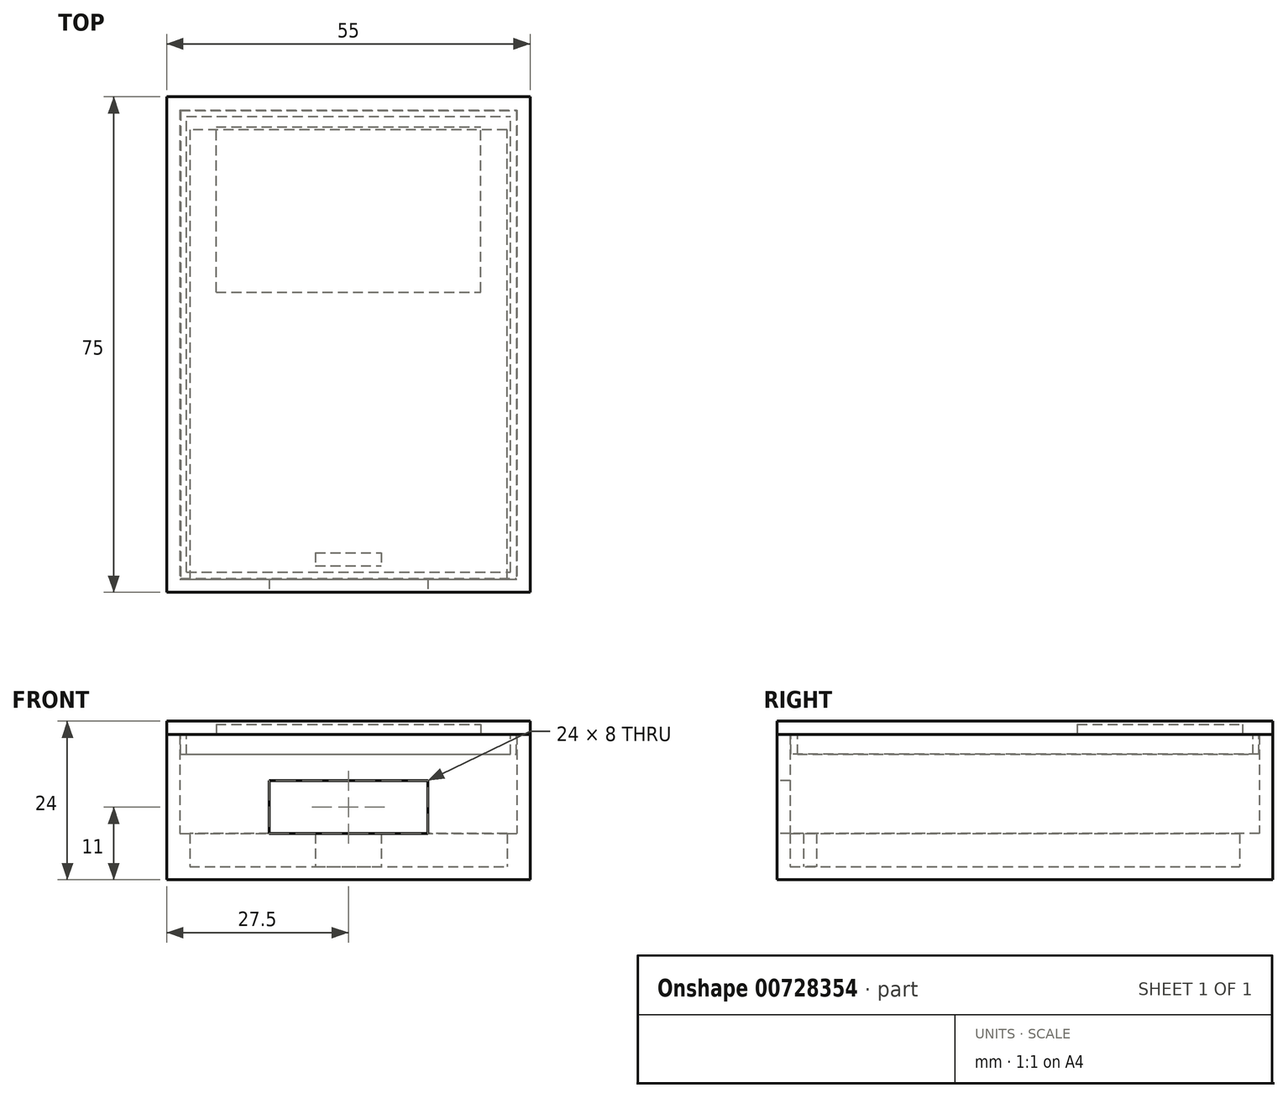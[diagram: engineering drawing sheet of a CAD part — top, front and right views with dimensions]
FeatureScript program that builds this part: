
annotation { "Feature Type Name" : "Feature", "Feature Type Description" : "" }
export const myFeature = defineFeature(function(context is Context, id is Id, definition is map)
    precondition{}
    {
        {
            var Q0;
            Q0=qCreatedBy(makeId("Top.planeOp"),FACE);
            var sketch = newSketch(context, id + "F0", { "sketchPlane" : qUnion([Q0])});
            skLineSegment(sketch, "E0.bottom", {"start": v(-27.5, 37.5) * mm, "end": v(27.5, 37.5) * mm});
            skLineSegment(sketch, "E0.top", {"start": v(-27.5, -37.5) * mm, "end": v(27.5, -37.5) * mm});
            skLineSegment(sketch, "E0.left", {"start": v(-27.5, 37.5) * mm, "end": v(-27.5, -37.5) * mm});
            skLineSegment(sketch, "E0.right", {"start": v(27.5, 37.5) * mm, "end": v(27.5, -37.5) * mm});
            skSolve(sketch);
        }
        {
            var Q0;
            Q0 = qSketchRegion(id + "F0", true);
            extrude(context, id + "F1", {"entities" : qUnion([Q0]), "depth" : 2 * mm, "offsetDistance" : 25 * mm});
        }
        {
            var Q0;
            Q0=makeQuery(id+"F1.opExtrude","CAP_FACE",FACE,{"disambiguationData":[OSD([sQuery(id+"F0.wireOp",EDGE,"E0.bottom"),sQuery(id+"F0.wireOp",EDGE,"E0.top"),sQuery(id+"F0.wireOp",EDGE,"E0.left"),sQuery(id+"F0.wireOp",EDGE,"E0.right")])],"isStart":false});
            var sketch = newSketch(context, id + "F2", { "sketchPlane" : qUnion([Q0])});
            skLineSegment(sketch, "E1.bottom", {"start": v(-27.5, 37.5) * mm, "end": v(27.5, 37.5) * mm});
            skLineSegment(sketch, "E1.top", {"start": v(-27.5, -37.5) * mm, "end": v(27.5, -37.5) * mm});
            skLineSegment(sketch, "E1.left", {"start": v(-27.5, 37.5) * mm, "end": v(-27.5, -37.5) * mm});
            skLineSegment(sketch, "E1.right", {"start": v(27.5, 37.5) * mm, "end": v(27.5, -37.5) * mm});
            skLineSegment(sketch, "E2.bottom", {"start": v(-25.5, 35.5) * mm, "end": v(25.5, 35.5) * mm});
            skLineSegment(sketch, "E2.top", {"start": v(-25.5, -35.5) * mm, "end": v(25.5, -35.5) * mm});
            skLineSegment(sketch, "E2.left", {"start": v(-25.5, 35.5) * mm, "end": v(-25.5, -35.5) * mm});
            skLineSegment(sketch, "E2.right", {"start": v(25.5, 35.5) * mm, "end": v(25.5, -35.5) * mm});
            skSolve(sketch);
        }
        {
            var Q0;
            Q0 = qSketchRegion(id + "F2", true);
            extrude(context, id + "F3", {"entities" : qUnion([Q0]), "operationType" : NewBodyOperationType.ADD, "depth" : 20 * mm, "offsetDistance" : 25 * mm});
        }
        {
            var Q0;
            Q0=makeQuery(id+"F1.opExtrude","CAP_FACE",FACE,{"disambiguationData":[OSD([sQuery(id+"F0.wireOp",EDGE,"E0.bottom"),sQuery(id+"F0.wireOp",EDGE,"E0.top"),sQuery(id+"F0.wireOp",EDGE,"E0.left"),sQuery(id+"F0.wireOp",EDGE,"E0.right")])],"isStart":false});
            var sketch = newSketch(context, id + "F4", { "sketchPlane" : qUnion([Q0])});
            skLineSegment(sketch, "E3", {"start": v(-25.5, -35.5) * mm, "end": v(-25.5, 35.5) * mm});
            skLineSegment(sketch, "E4", {"start": v(-25.5, 35.5) * mm, "end": v(25.5, 35.5) * mm});
            skLineSegment(sketch, "E5", {"start": v(25.5, 35.5) * mm, "end": v(25.5, -35.5) * mm});
            skLineSegment(sketch, "E6", {"start": v(25.5, -35.5) * mm, "end": v(24, -35.5) * mm});
            skLineSegment(sketch, "E7", {"start": v(24, -35.5) * mm, "end": v(24, 32.5) * mm});
            skLineSegment(sketch, "E8", {"start": v(24, 32.5) * mm, "end": v(-24, 32.5) * mm});
            skLineSegment(sketch, "E9", {"start": v(-24, 32.5) * mm, "end": v(-24, -35.5) * mm});
            skLineSegment(sketch, "E10", {"start": v(-24, -35.5) * mm, "end": v(-25.5, -35.5) * mm});
            skLineSegment(sketch, "E11", {"start": v(0, 32.5) * mm, "end": v(0, 35.5) * mm, "construction": true});
            skLineSegment(sketch, "E12.bottom", {"start": v(-5, -31.5) * mm, "end": v(5, -31.5) * mm});
            skLineSegment(sketch, "E12.top", {"start": v(-5, -33.5) * mm, "end": v(5, -33.5) * mm});
            skLineSegment(sketch, "E12.left", {"start": v(-5, -31.5) * mm, "end": v(-5, -33.5) * mm});
            skLineSegment(sketch, "E12.right", {"start": v(5, -31.5) * mm, "end": v(5, -33.5) * mm});
            skLineSegment(sketch, "E13", {"start": v(0, 32.5) * mm, "end": v(0, -31.5) * mm, "construction": true});
            skSolve(sketch);
        }
        {
            var Q0;
            Q0 = qSketchRegion(id + "F4", true);
            extrude(context, id + "F5", {"entities" : qUnion([Q0]), "operationType" : NewBodyOperationType.ADD, "depth" : 5 * mm, "offsetDistance" : 25 * mm});
        }
        {
            var Q0;
            Q0=makeQuery(id+"F5.opExtrude","CAP_FACE",FACE,{"disambiguationData":[OSD([sQuery(id+"F4.wireOp",EDGE,"E12.bottom"),sQuery(id+"F4.wireOp",EDGE,"E12.top"),sQuery(id+"F4.wireOp",EDGE,"E12.left"),sQuery(id+"F4.wireOp",EDGE,"E12.right")])],"isStart":false});
            var sketch = newSketch(context, id + "F6", { "sketchPlane" : qUnion([Q0])});
            skLineSegment(sketch, "E14.bottom", {"start": v(-12, -22.95) * mm, "end": v(12, -22.95) * mm});
            skLineSegment(sketch, "E14.top", {"start": v(-12, -43.26) * mm, "end": v(12, -43.26) * mm});
            skLineSegment(sketch, "E14.left", {"start": v(-12, -22.95) * mm, "end": v(-12, -43.26) * mm});
            skLineSegment(sketch, "E14.right", {"start": v(12, -22.95) * mm, "end": v(12, -43.26) * mm});
            skSolve(sketch);
        }
        {
            var Q0;
            Q0 = qSketchRegion(id + "F6", true);
            extrude(context, id + "F7", {"entities" : qUnion([Q0]), "operationType" : NewBodyOperationType.REMOVE, "depth" : 8 * mm, "offsetDistance" : 25 * mm});
        }
        {
            var Q0;
            Q0=makeQuery(id+"F3.opExtrude","CAP_FACE",FACE,{"disambiguationData":[OSD([sQuery(id+"F2.wireOp",EDGE,"E1.bottom"),sQuery(id+"F2.wireOp",EDGE,"E1.top"),sQuery(id+"F2.wireOp",EDGE,"E1.left"),sQuery(id+"F2.wireOp",EDGE,"E1.right"),sQuery(id+"F2.wireOp",EDGE,"E2.bottom"),sQuery(id+"F2.wireOp",EDGE,"E2.top"),sQuery(id+"F2.wireOp",EDGE,"E2.left"),sQuery(id+"F2.wireOp",EDGE,"E2.right")])],"isStart":false});
            var sketch = newSketch(context, id + "F8", { "sketchPlane" : qUnion([Q0])});
            skLineSegment(sketch, "E15.bottom", {"start": v(-27.5, 37.5) * mm, "end": v(27.5, 37.5) * mm});
            skLineSegment(sketch, "E15.top", {"start": v(-27.5, -37.5) * mm, "end": v(27.5, -37.5) * mm});
            skLineSegment(sketch, "E15.left", {"start": v(-27.5, 37.5) * mm, "end": v(-27.5, -37.5) * mm});
            skLineSegment(sketch, "E15.right", {"start": v(27.5, 37.5) * mm, "end": v(27.5, -37.5) * mm});
            skSolve(sketch);
        }
        {
            var Q0;
            Q0 = qSketchRegion(id + "F8", true);
            extrude(context, id + "F9", {"entities" : qUnion([Q0]), "depth" : 2 * mm, "offsetDistance" : 25 * mm});
        }
        {
            var Q0;
            Q0=makeQuery(id+"F9.opExtrude","CAP_FACE",FACE,{"disambiguationData":[OSD([sQuery(id+"F8.wireOp",EDGE,"E15.bottom"),sQuery(id+"F8.wireOp",EDGE,"E15.top"),sQuery(id+"F8.wireOp",EDGE,"E15.left"),sQuery(id+"F8.wireOp",EDGE,"E15.right")])],"isStart":true});
            var sketch = newSketch(context, id + "F10", { "sketchPlane" : qUnion([Q0])});
            skLineSegment(sketch, "E16.bottom", {"start": v(-25.4, -35.4) * mm, "end": v(25.4, -35.4) * mm});
            skLineSegment(sketch, "E16.top", {"start": v(-25.4, 35.4) * mm, "end": v(25.4, 35.4) * mm});
            skLineSegment(sketch, "E16.left", {"start": v(-25.4, -35.4) * mm, "end": v(-25.4, 35.4) * mm});
            skLineSegment(sketch, "E16.right", {"start": v(25.4, -35.4) * mm, "end": v(25.4, 35.4) * mm});
            skPoint(sketch, "E17.0", {"position": v(-27.5, 37.5) * mm});
            skLineSegment(sketch, "E18.0.0", {"start": v(-25.5, -35.5) * mm, "end": v(-25.5, 35.5) * mm, "construction": true});
            skLineSegment(sketch, "E18.0.1", {"start": v(-25.5, 35.5) * mm, "end": v(25.5, 35.5) * mm, "construction": true});
            skLineSegment(sketch, "E18.0.2", {"start": v(25.5, 35.5) * mm, "end": v(25.5, -35.5) * mm, "construction": true});
            skLineSegment(sketch, "E18.0.3", {"start": v(25.5, -35.5) * mm, "end": v(-25.5, -35.5) * mm, "construction": true});
            skLineSegment(sketch, "E19.bottom", {"start": v(-24.5, 34.4) * mm, "end": v(24.5, 34.4) * mm});
            skLineSegment(sketch, "E19.top", {"start": v(-24.5, -34.5) * mm, "end": v(24.5, -34.5) * mm});
            skLineSegment(sketch, "E19.left", {"start": v(-24.5, 34.4) * mm, "end": v(-24.5, -34.5) * mm});
            skLineSegment(sketch, "E19.right", {"start": v(24.5, 34.4) * mm, "end": v(24.5, -34.5) * mm});
            skSolve(sketch);
        }
        {
            var Q0;
            Q0 = qSketchRegion(id + "F10", true);
            extrude(context, id + "F11", {"entities" : qUnion([Q0]), "operationType" : NewBodyOperationType.ADD, "depth" : 3 * mm, "offsetDistance" : 25 * mm});
        }
        {
            var Q0;
            Q0=makeQuery(id+"F9.opExtrude","CAP_FACE",FACE,{"disambiguationData":[OSD([sQuery(id+"F8.wireOp",EDGE,"E15.bottom"),sQuery(id+"F8.wireOp",EDGE,"E15.top"),sQuery(id+"F8.wireOp",EDGE,"E15.left"),sQuery(id+"F8.wireOp",EDGE,"E15.right")])],"isStart":true});
            var sketch = newSketch(context, id + "F12", { "sketchPlane" : qUnion([Q0])});
            skLineSegment(sketch, "E20.bottom", {"start": v(-20, -7.94) * mm, "end": v(20, -7.94) * mm});
            skLineSegment(sketch, "E20.top", {"start": v(-20, -32.94) * mm, "end": v(20, -32.94) * mm});
            skLineSegment(sketch, "E20.left", {"start": v(-20, -7.94) * mm, "end": v(-20, -32.94) * mm});
            skLineSegment(sketch, "E20.right", {"start": v(20, -7.94) * mm, "end": v(20, -32.94) * mm});
            skSolve(sketch);
        }
        {
            var Q0;
            Q0 = qSketchRegion(id + "F12", true);
            extrude(context, id + "F13", {"entities" : qUnion([Q0]), "operationType" : NewBodyOperationType.REMOVE, "endBound" : BoundingType.UP_TO_NEXT, "oppositeDirection" : true, "depth" : 25 * mm, "hasOffset" : true, "offsetDistance" : 0.5 * mm});
        }
    });
